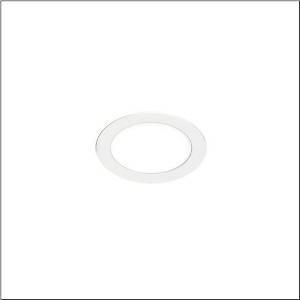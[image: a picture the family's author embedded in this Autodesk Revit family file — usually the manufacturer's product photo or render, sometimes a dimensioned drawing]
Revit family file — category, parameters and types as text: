
# Revit family: lunis_41_flat_51dr107dgba
name_source: partatom
category: Lighting Fixtures
units: mm (PartAtom-declared; Revit-internal decimal feet)

## family parameters
Cut with Voids When Loaded = No
Host = Face
Light Source = No
Part Type = Normal
Room Calculation Point = No
Round Connector Dimension = Use Diameter
Shared = No

## types (1)
- --- (1 x LED, 1360 lm, 15 W, 4000K)
    Apparent Load = 15 VA
    CIE Flux Codes = 49 80 96 100 100
    Color Rendering = 80
    Color Temperature = 4000K
    Default Elevation = 1800 mm
    Description = Lunis 41,  Flat, downlight, light emission: direct distribution, LED rated luminous flux: 1.250lm, light colour: 830/840, control gear: ECG, mains connection: 230V, AC, 50/60Hz, housing, round, of aluminium, coated, traffic white (RAL 9016), diameter: 170mm, protection rating (complete): IP20, protection rating (on room side): IP44, insulation class (complete): insulation class II (safety insulation), certification: CE, permissible ambient temperature for indoor applications: -20..+40°C, packaging unit: 1 piece
    Height = 0 mm  [stored 0 ft]
    Lamp = 1 x LED
    Lamp Light Flux = 1360 lm
    Lamp Power = 15 W
    Lamp count = 1
    Length = 170 mm
    Luminous efficacy = 91 lm/W
    Manufacturer = Siteco
    ModVariant = No
    Model = 51DR107DGBA
    Mounting Place = Ceiling
    Mounting Type = Recessed
    Number of Poles = 1
    OnlyDefault = Yes
    Power Factor = 1
    Product Name = Lunis 41 Flat
    Product group = downlight
    ProductGroupID = 400
    Protection Class = Protection class II
    Protection Degree = IP 20
    RLX_Detail_Level = 1
    RLX_Emergency_Light_Flux = 0 lm
    RLX_Emergency_Type = 0
    RLX_Emergency_Type_DB = No
    RlxData = <blob elided: 24237 chars, md5=daf17eee>
    Socket = socket
    Standby Power = 0 W
    System Light Flux = 1360 lm
    System Power = 15 W
    Type Comments = factory setting: colour temperature 4000K
    Type Image = l_1340921.jpg
    URL = http://relux.com
    VarID = @adj_195570
    Voltage = 0 V
    Weight = 0.00 kg
    Width = 0 mm  [stored 0 ft]

note: [stored X ft] marks values corroborated as IEEE doubles in the binary element streams (Revit-internal decimal feet)

## geometry (parser evidence)
native form markers: Blend x4, Sweep x9
no freeform markers — native parametric forms only
